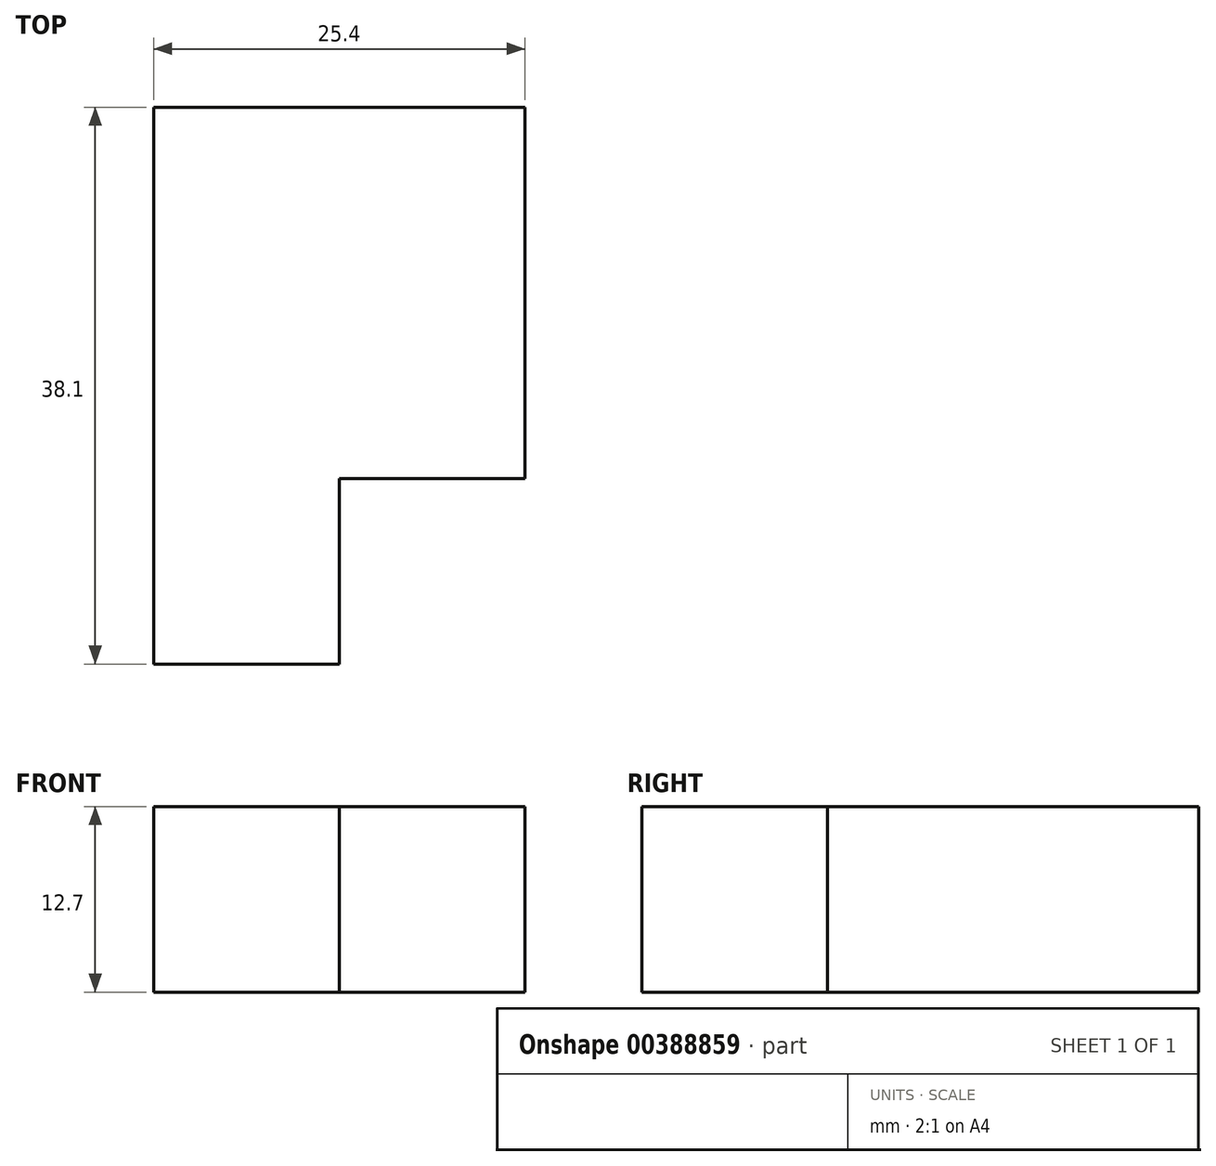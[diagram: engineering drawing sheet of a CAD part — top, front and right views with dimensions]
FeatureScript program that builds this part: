
annotation { "Feature Type Name" : "Feature", "Feature Type Description" : "" }
export const myFeature = defineFeature(function(context is Context, id is Id, definition is map)
    precondition{}
    {
        {
            var Q0;
            Q0=qCreatedBy(makeId("Top.planeOp"),FACE);
            var sketch = newSketch(context, id + "F0", { "sketchPlane" : qUnion([Q0])});
            skLineSegment(sketch, "E0.top", {"start": v(0, 25.4) * mm, "end": v(25.4, 25.4) * mm});
            skLineSegment(sketch, "E0.left", {"start": v(0, 0) * mm, "end": v(0, 25.4) * mm});
            skLineSegment(sketch, "E0.right", {"start": v(25.4, 0) * mm, "end": v(25.4, 25.4) * mm});
            skLineSegment(sketch, "E1.top", {"start": v(0, -12.7) * mm, "end": v(12.7, -12.7) * mm});
            skLineSegment(sketch, "E1.left", {"start": v(0, 0) * mm, "end": v(0, -12.7) * mm});
            skLineSegment(sketch, "E1.right", {"start": v(12.7, 0) * mm, "end": v(12.7, -12.7) * mm});
            skLineSegment(sketch, "E2", {"start": v(12.7, 0) * mm, "end": v(25.4, 0) * mm});
            skSolve(sketch);
        }
        {
            var Q0;
            Q0=makeQuery(id+"F0.imprint","IMPRINT",FACE,{"disambiguationData":[TD([[makeQuery(id+"F0.imprint","IMPRINT",EDGE,{"derivedFrom":sQuery(id+"F0.wireOp",EDGE,"E0.top")}),-1.0]])]});
            extrude(context, id + "F1", {"entities" : qUnion([Q0]), "depth" : 12.7 * mm});
        }
    });
